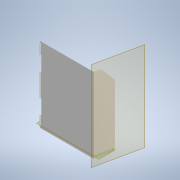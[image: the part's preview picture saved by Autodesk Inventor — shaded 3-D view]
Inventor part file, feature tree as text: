
AUTODESK INVENTOR PART (.ipt)
format: ipt  version: 2021 (Build 250183000, 183)  size: 190,464 bytes
history: native  units: mm
features: sketch x6, extrude x5, fillet x5, plane x2, other x2, hole x1
ambient origin geometry x8: Origin, YZ Plane, XZ Plane, XY Plane, X Axis, Y Axis, Z Axis, Center Point
bodies: Solid1 (feature_tree)
feature tree (21):
  extrude  "Extrusion1"  Depth=1300.0mm
  extrude  "Extrusion2"  Depth=20.0mm
  extrude  "Extrusion3"  Depth=2.5mm
  plane  "Work Plane1"
  extrude  "Extrusion4"  Depth=650.0mm
  fillet  "Fillet1"  Radius=550.0mm
  fillet  "Fillet2"  Radius=200.0mm
  fillet  "Fillet3"  Radius=200.0mm
  plane  "Work Plane2"
  extrude  "Extrusion5"  Depth=1100.0mm TaperAngle=0.0deg
  fillet  "Fillet4"  Radius=1100.0mm
  fillet  "Fillet5"  Radius=309.0mm
  hole  "Hole1"  [1 undecoded]
  sketch  "Sketch1"  dims[d0=925.0mm d1=1300.0mm]
  sketch  "Sketch2"  dims[d2=3.0mm d3=0.0mm d4=20.0mm]
  sketch  "Sketch3"  dims[d5=5.0mm d6=2.5mm]
  sketch  "Sketch4"  dims[d7=1250.0mm d8=0.0mm d9=650.0mm d10=550.0mm d11=200.0mm d12=200.0mm]
  sketch  "Sketch5"  dims[d14=40.0mm d15=30.0mm d16=0.0mm d17=1100.0mm d18=530.0mm d19=309.0mm]
  sketch  "Sketch6"  dims[d20=22.68928mm d21=3.0mm d22=0.0mm d23=6.0mm d24=2.0mm d25=50.0mm d26=1061.7mm d27=-50.0mm d28=18.0mm d29=20.0mm d30=280.0mm d31=10.0mm d32=0.0mm d33=6.0mm d34=6.0mm d35=9.0mm d36=9.0mm d37=8.0mm d38=6.0mm d39=4.0mm d40=2.0mm d41=90.0deg d42=8.0mm d43=20.594885mm]
  other  "cover_final_assembly.iam"
  other  "wheelchair_box_extended:1"
note: 1 required parameter value undecoded (feature->parameter linkage not recoverable at this tier; creation-order binding heuristic only, values carry confidence <= 0.55)
